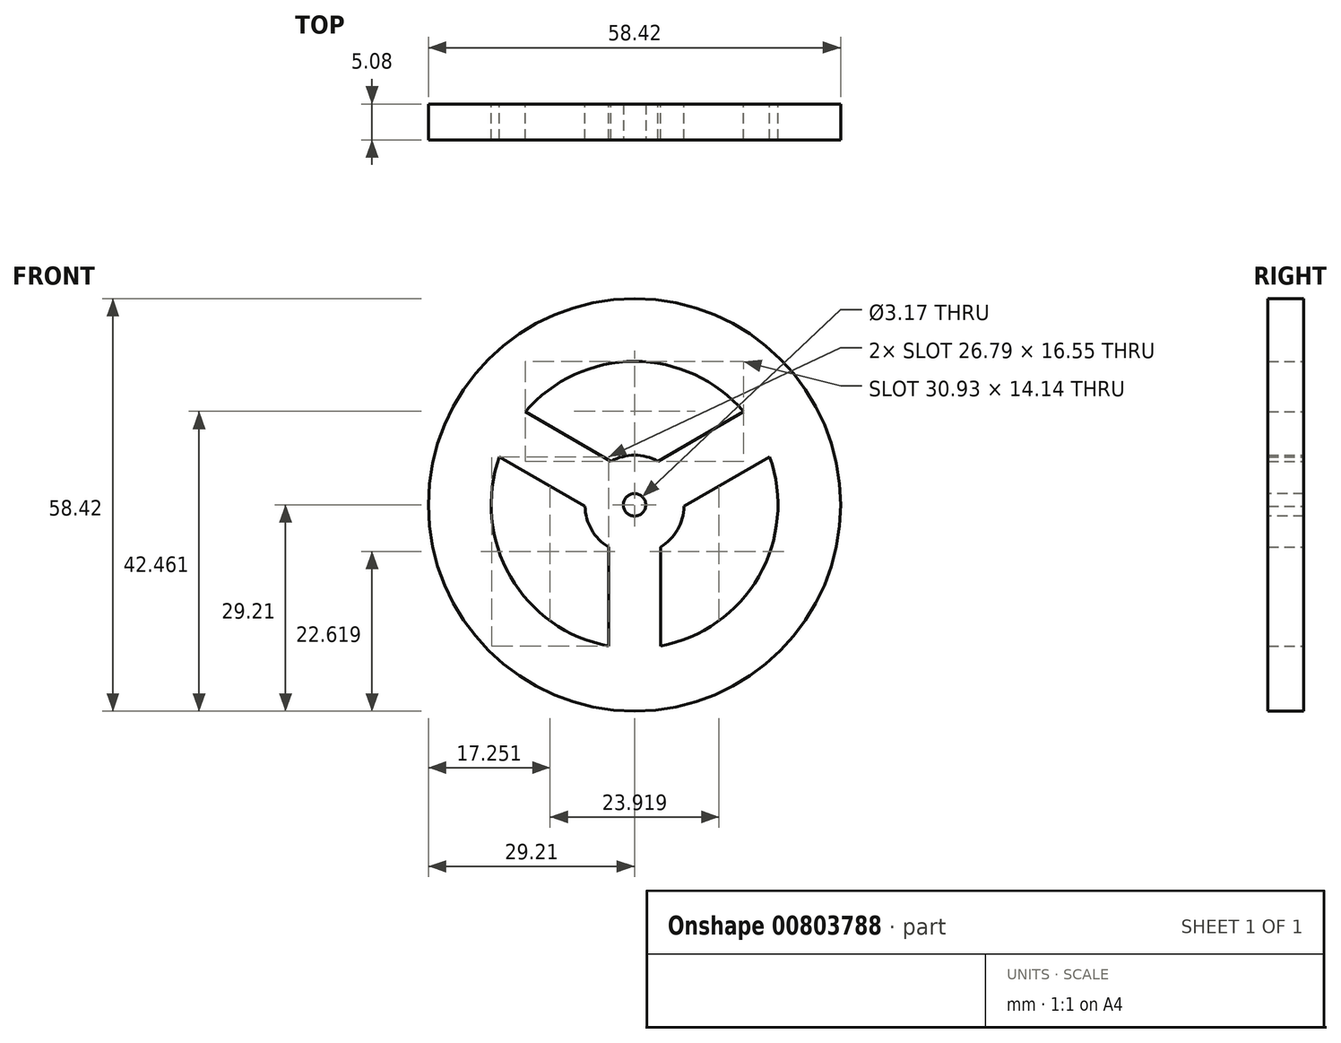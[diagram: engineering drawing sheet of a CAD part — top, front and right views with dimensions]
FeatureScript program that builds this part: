
annotation { "Feature Type Name" : "Feature", "Feature Type Description" : "" }
export const myFeature = defineFeature(function(context is Context, id is Id, definition is map)
    precondition{}
    {
        {
            var Q0;
            Q0=qCreatedBy(makeId("Front.planeOp"),FACE);
            var sketch = newSketch(context, id + "F0", { "sketchPlane" : qUnion([Q0])});
            skCircle(sketch, "E0", {"center": v(0, 0) * mm, "radius": 29.21 * mm});
            skCircle(sketch, "E1", {"center": v(0, 0) * mm, "radius": 20.32 * mm});
            skCircle(sketch, "E2", {"center": v(0, 0) * mm, "radius": 7.03 * mm});
            skLineSegment(sketch, "E3", {"start": v(-3.68, -5.98) * mm, "end": v(-3.68, -19.98) * mm});
            skLineSegment(sketch, "E4", {"start": v(3.68, -5.98) * mm, "end": v(3.68, -19.98) * mm});
            skLineSegment(sketch, "E5", {"start": v(0, 0) * mm, "end": v(0, -20.32) * mm});
            skLineSegment(sketch, "E6.1.0", {"start": v(7.02, -0.2) * mm, "end": v(19.15, 6.8) * mm});
            skLineSegment(sketch, "E6.1.1", {"start": v(3.34, 6.18) * mm, "end": v(15.46, 13.18) * mm});
            skLineSegment(sketch, "E6.2.0", {"start": v(-3.34, 6.18) * mm, "end": v(-15.46, 13.18) * mm});
            skLineSegment(sketch, "E6.2.1", {"start": v(-7.02, -0.2) * mm, "end": v(-19.15, 6.8) * mm});
            skSolve(sketch);
        }
        {
            var Q0;
            Q0=makeQuery(id+"F0.imprint","IMPRINT",FACE,{"disambiguationData":[TD([[makeQuery(id+"F0.imprint","IMPRINT",EDGE,{"derivedFrom":sQuery(id+"F0.wireOp",EDGE,"E0")}),1.0]])]});
            var Q1;
            {var subQ0=sQuery(id+"F0.wireOp",EDGE,"E6.2.0");Q1=makeQuery(id+"F0.imprint","IMPRINT",FACE,{"disambiguationData":[TD([[makeQuery(id+"F0.imprint","IMPRINT",EDGE,{"derivedFrom":subQ0}),1.0]])]});}
            var Q2;
            {var subQ0=sQuery(id+"F0.wireOp",EDGE,"E2");var subQ5=makeQuery(id+"F0.imprint","INTERSECT",VERTEX,{"derivedFrom":[subQ0,sQuery(id+"F0.wireOp",EDGE,"E6.1.1")]});Q2=makeQuery(id+"F0.imprint","IMPRINT",FACE,{"disambiguationData":[TD([[makeQuery(id+"F0.imprint","IMPRINT",EDGE,{"disambiguationData":[TD([[subQ5,-1.0]])],"derivedFrom":subQ0}),1.0]])]});}
            var Q3;
            {var subQ0=sQuery(id+"F0.wireOp",EDGE,"E4");Q3=makeQuery(id+"F0.imprint","IMPRINT",FACE,{"disambiguationData":[TD([[makeQuery(id+"F0.imprint","IMPRINT",EDGE,{"derivedFrom":subQ0}),-1.0]])]});}
            var Q4;
            {var subQ0=sQuery(id+"F0.wireOp",EDGE,"E6.1.0");Q4=makeQuery(id+"F0.imprint","IMPRINT",FACE,{"disambiguationData":[TD([[makeQuery(id+"F0.imprint","IMPRINT",EDGE,{"derivedFrom":subQ0}),1.0]])]});}
            var Q5;
            {var subQ0=sQuery(id+"F0.wireOp",EDGE,"E3");Q5=makeQuery(id+"F0.imprint","IMPRINT",FACE,{"disambiguationData":[TD([[makeQuery(id+"F0.imprint","IMPRINT",EDGE,{"derivedFrom":subQ0}),1.0]])]});}
            extrude(context, id + "F1", {"entities" : qUnion([Q0, Q1, Q2, Q3, Q4, Q5]), "depth" : 5.08 * mm, "offsetDistance" : 25.4 * mm});
        }
        {
            var Q0;
            Q0=makeQuery(id+"F1.opExtrude","CAP_FACE",FACE,{"disambiguationData":[OSD([sQuery(id+"F0.wireOp",EDGE,"E0")])],"isStart":false});
            var sketch = newSketch(context, id + "F2", { "sketchPlane" : qUnion([Q0])});
            skCircle(sketch, "E7", {"center": v(0, 0) * mm, "radius": 1.59 * mm});
            skSolve(sketch);
        }
        {
            var Q0;
            Q0=makeQuery(id+"F2.imprint","IMPRINT",FACE,{"disambiguationData":[TD([[makeQuery(id+"F2.imprint","IMPRINT",EDGE,{"derivedFrom":sQuery(id+"F2.wireOp",EDGE,"E7")}),1.0]])]});
            extrude(context, id + "F3", {"entities" : qUnion([Q0]), "operationType" : NewBodyOperationType.REMOVE, "oppositeDirection" : true, "depth" : 25.4 * mm, "offsetDistance" : 25.4 * mm});
        }
    });
